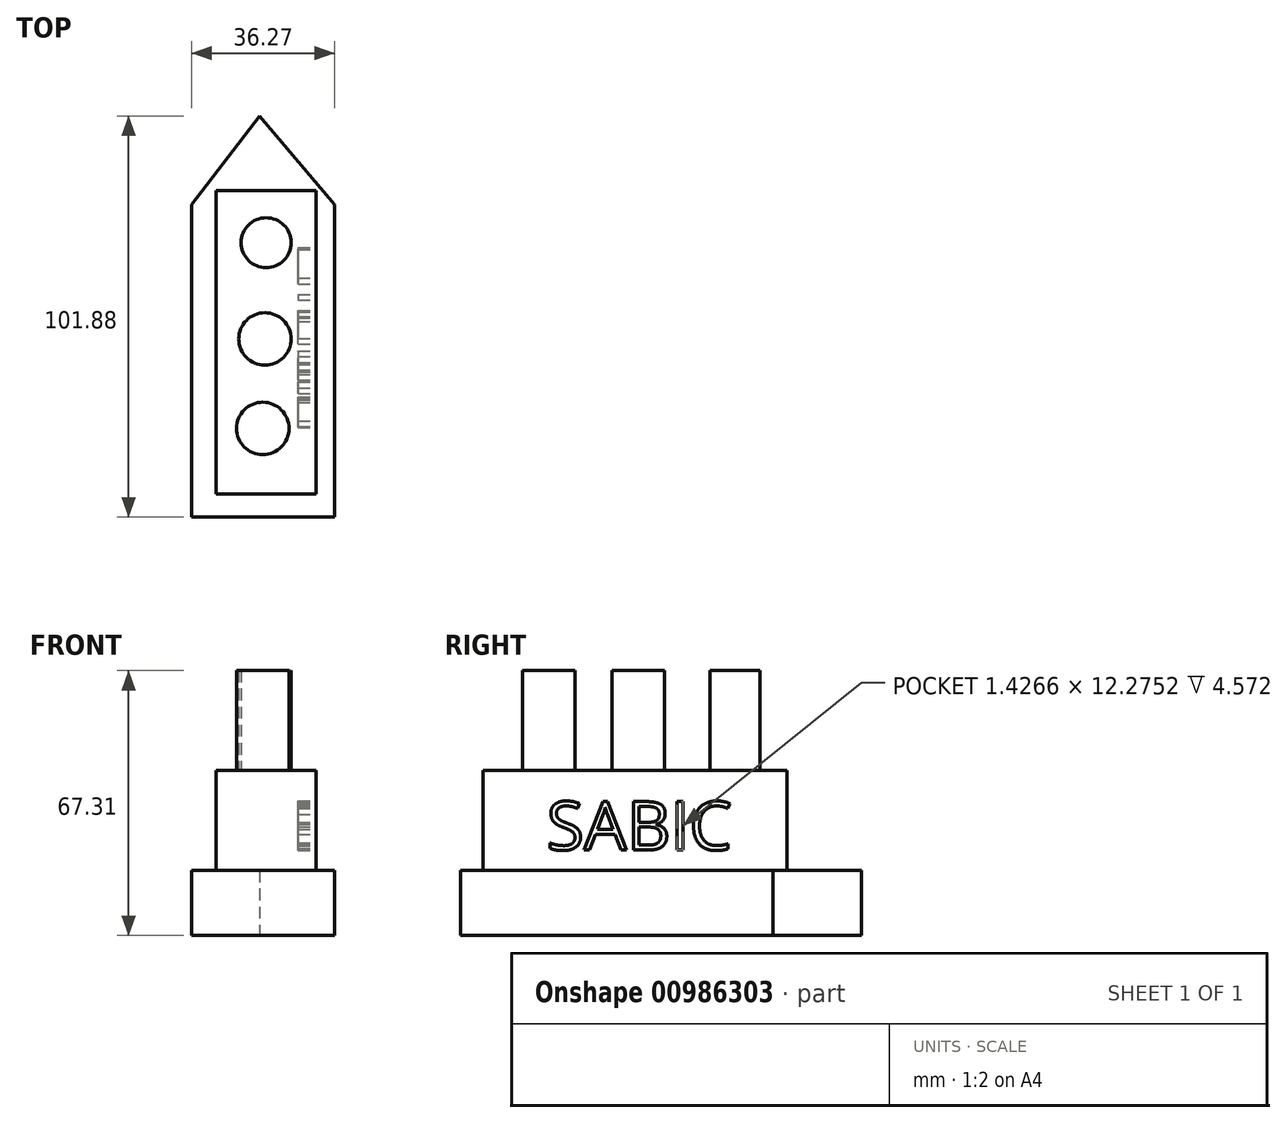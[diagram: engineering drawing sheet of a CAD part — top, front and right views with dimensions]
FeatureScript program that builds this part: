
annotation { "Feature Type Name" : "Feature", "Feature Type Description" : "" }
export const myFeature = defineFeature(function(context is Context, id is Id, definition is map)
    precondition{}
    {
        {
            var Q0;
            Q0=qCreatedBy(makeId("Top.planeOp"),FACE);
            var sketch = newSketch(context, id + "F0", { "sketchPlane" : qUnion([Q0])});
            skLineSegment(sketch, "E0", {"start": v(1.1, 56.5) * mm, "end": v(-16.18, 34.06) * mm});
            skLineSegment(sketch, "E1", {"start": v(-16.18, 34.06) * mm, "end": v(1.1, 56.5) * mm});
            skLineSegment(sketch, "E2", {"start": v(1.1, 56.5) * mm, "end": v(20.09, 34.06) * mm});
            skLineSegment(sketch, "E3", {"start": v(20.09, 34.06) * mm, "end": v(20.09, -45.38) * mm});
            skLineSegment(sketch, "E4", {"start": v(-16.18, 34.06) * mm, "end": v(-16.18, -45.38) * mm});
            skLineSegment(sketch, "E5", {"start": v(-16.18, -45.38) * mm, "end": v(20.09, -45.38) * mm});
            skSolve(sketch);
        }
        {
            var Q0;
            Q0 = qSketchRegion(id + "F0", true);
            extrude(context, id + "F1", {"entities" : qUnion([Q0]), "depth" : 16.5 * mm, "offsetDistance" : 25.4 * mm});
        }
        {
            var Q0;
            Q0=makeQuery(id+"F1.opExtrude","CAP_FACE",FACE,{"disambiguationData":[OSD([sQuery(id+"F0.wireOp",EDGE,"E1"),sQuery(id+"F0.wireOp",EDGE,"E2"),sQuery(id+"F0.wireOp",EDGE,"E3"),sQuery(id+"F0.wireOp",EDGE,"E4"),sQuery(id+"F0.wireOp",EDGE,"E5")])],"isStart":false});
            var sketch = newSketch(context, id + "F2", { "sketchPlane" : qUnion([Q0])});
            skLineSegment(sketch, "E6", {"start": v(-9.93, 37.56) * mm, "end": v(-9.93, -39.57) * mm});
            skLineSegment(sketch, "E7", {"start": v(-9.93, 37.56) * mm, "end": v(15.47, 37.56) * mm});
            skLineSegment(sketch, "E8", {"start": v(15.47, 37.56) * mm, "end": v(15.47, -39.57) * mm});
            skLineSegment(sketch, "E9", {"start": v(-11.03, -39.57) * mm, "end": v(15.47, -39.57) * mm});
            skSolve(sketch);
        }
        {
            var Q0;
            Q0 = qSketchRegion(id + "F2", true);
            extrude(context, id + "F3", {"entities" : qUnion([Q0]), "operationType" : NewBodyOperationType.ADD, "depth" : 25.4 * mm, "offsetDistance" : 25.4 * mm});
        }
        {
            var Q0;
            Q0=makeQuery(id+"F3.opExtrude","SWEPT_FACE",FACE,{"disambiguationData":[OSD([sQuery(id+"F2.wireOp",EDGE,"E8")])]});
            var sketch = newSketch(context, id + "F4", { "sketchPlane" : qUnion([Q0])});
            skText(sketch, "E10", { "text": "SABIC", "fontName": "OpenSans-Regular.ttf"});
            const initialGuessF4  = {"E10": [-0.02346, 0.02173, 1, 0, 0.01238]};
            skSetInitialGuess(sketch, initialGuessF4);
            skSolve(sketch);
        }
        {
            var Q0;
            Q0 = qSketchRegion(id + "F4", true);
            extrude(context, id + "F5", {"entities" : qUnion([Q0]), "operationType" : NewBodyOperationType.REMOVE, "oppositeDirection" : true, "depth" : 4.57 * mm, "offsetDistance" : 25.4 * mm});
        }
        {
            var Q0;
            Q0=makeQuery(id+"F3.opExtrude","CAP_FACE",FACE,{"disambiguationData":[OSD([sQuery(id+"F2.wireOp",EDGE,"E6"),sQuery(id+"F2.wireOp",EDGE,"E7"),sQuery(id+"F2.wireOp",EDGE,"E8"),sQuery(id+"F2.wireOp",EDGE,"E9")])],"isStart":false});
            var sketch = newSketch(context, id + "F6", { "sketchPlane" : qUnion([Q0])});
            skCircle(sketch, "E11", {"center": v(2.73, 24.32) * mm, "radius": 6.35 * mm});
            skCircle(sketch, "E12", {"center": v(2.45, -0.14) * mm, "radius": 6.67 * mm});
            skCircle(sketch, "E13", {"center": v(1.87, -22.88) * mm, "radius": 6.67 * mm});
            skSolve(sketch);
        }
        {
            var Q0;
            Q0 = qSketchRegion(id + "F6", true);
            extrude(context, id + "F7", {"entities" : qUnion([Q0]), "operationType" : NewBodyOperationType.ADD, "depth" : 25.4 * mm, "offsetDistance" : 25.4 * mm});
        }
    });
